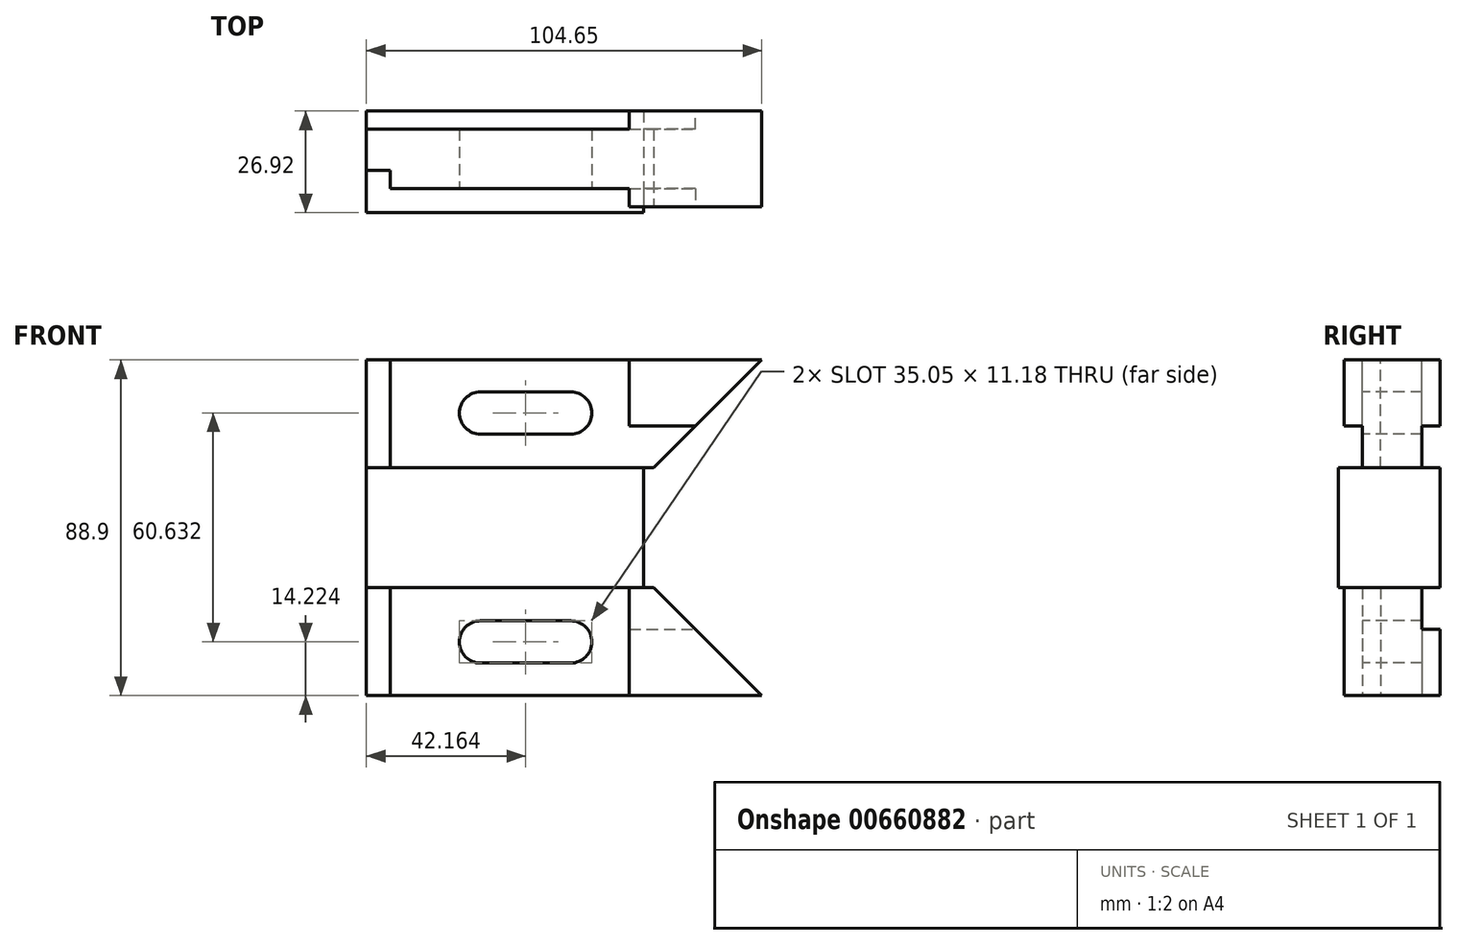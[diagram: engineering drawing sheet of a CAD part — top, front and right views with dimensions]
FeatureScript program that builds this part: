
annotation { "Feature Type Name" : "Feature", "Feature Type Description" : "" }
export const myFeature = defineFeature(function(context is Context, id is Id, definition is map)
    precondition{}
    {
        {
            var Q0;
            Q0=qCreatedBy(makeId("Right.planeOp"),FACE);
            var sketch = newSketch(context, id + "F0", { "sketchPlane" : qUnion([Q0])});
            skLineSegment(sketch, "E0", {"start": v(0, 0) * mm, "end": v(25.4, 0) * mm});
            skLineSegment(sketch, "E1", {"start": v(25.4, 0) * mm, "end": v(25.4, 28.58) * mm});
            skLineSegment(sketch, "E2", {"start": v(0, 0) * mm, "end": v(0, 28.58) * mm});
            skLineSegment(sketch, "E3", {"start": v(25.4, 60.33) * mm, "end": v(25.4, 88.9) * mm});
            skLineSegment(sketch, "E4", {"start": v(0, 60.33) * mm, "end": v(0, 88.9) * mm});
            skLineSegment(sketch, "E5", {"start": v(0, 88.9) * mm, "end": v(25.4, 88.9) * mm});
            skLineSegment(sketch, "E6", {"start": v(0, 28.58) * mm, "end": v(-1.52, 28.58) * mm});
            skLineSegment(sketch, "E7", {"start": v(-1.52, 28.58) * mm, "end": v(-1.52, 60.33) * mm});
            skLineSegment(sketch, "E8", {"start": v(0, 60.33) * mm, "end": v(-1.52, 60.33) * mm});
            skLineSegment(sketch, "E9", {"start": v(25.4, 60.33) * mm, "end": v(26.92, 60.33) * mm});
            skLineSegment(sketch, "E10", {"start": v(25.4, 28.58) * mm, "end": v(26.92, 28.58) * mm});
            skLineSegment(sketch, "E11", {"start": v(26.92, 60.33) * mm, "end": v(26.92, 28.58) * mm});
            skSolve(sketch);
        }
        {
            var Q0;
            Q0=qSketchRegion(id+"F0",true);
            extrude(context, id + "F1", {"entities" : qUnion([Q0]), "depth" : 104.65 * mm, "offsetDistance" : 25 * mm});
        }
        {
            var Q0;
            Q0=makeQuery(id+"F1.opExtrude","SWEPT_FACE",FACE,{"disambiguationData":[OSD([sQuery(id+"F0.wireOp",EDGE,"E5")])]});
            var sketch = newSketch(context, id + "F2", { "sketchPlane" : qUnion([Q0])});
            skLineSegment(sketch, "E12.0.0", {"start": v(0, 0) * mm, "end": v(0, -1.52) * mm});
            skLineSegment(sketch, "E12.0.1", {"start": v(0, -1.52) * mm, "end": v(104.65, -1.52) * mm});
            skLineSegment(sketch, "E12.0.2", {"start": v(104.65, -1.52) * mm, "end": v(104.65, 0) * mm});
            skLineSegment(sketch, "E12.0.3", {"start": v(104.65, 0) * mm, "end": v(0, 0) * mm});
            skLineSegment(sketch, "E13", {"start": v(0, -1.52) * mm, "end": v(0, 4.83) * mm});
            skLineSegment(sketch, "E14.0.0", {"start": v(0, 26.92) * mm, "end": v(0, 25.4) * mm});
            skLineSegment(sketch, "E14.0.1", {"start": v(0, 25.4) * mm, "end": v(104.65, 25.4) * mm});
            skLineSegment(sketch, "E14.0.2", {"start": v(104.65, 25.4) * mm, "end": v(104.65, 26.92) * mm});
            skLineSegment(sketch, "E14.0.3", {"start": v(104.65, 26.92) * mm, "end": v(0, 26.92) * mm});
            skLineSegment(sketch, "E15", {"start": v(0, 26.92) * mm, "end": v(0, 20.57) * mm});
            skLineSegment(sketch, "E16", {"start": v(0, 4.83) * mm, "end": v(0, 9.65) * mm});
            skLineSegment(sketch, "E17", {"start": v(0, 9.65) * mm, "end": v(6.35, 9.65) * mm});
            skLineSegment(sketch, "E18", {"start": v(6.35, 9.65) * mm, "end": v(6.35, 4.83) * mm});
            skLineSegment(sketch, "E19", {"start": v(6.35, 4.83) * mm, "end": v(69.6, 4.83) * mm});
            skLineSegment(sketch, "E20", {"start": v(0, 20.57) * mm, "end": v(69.6, 20.57) * mm});
            skLineSegment(sketch, "E21", {"start": v(69.6, 20.57) * mm, "end": v(69.6, 25.4) * mm});
            skLineSegment(sketch, "E22", {"start": v(69.6, 4.83) * mm, "end": v(69.6, 0) * mm});
            skLineSegment(sketch, "E23", {"start": v(0, -1.52) * mm, "end": v(73.4, -1.52) * mm});
            skLineSegment(sketch, "E24", {"start": v(73.4, -1.52) * mm, "end": v(73.4, 0) * mm});
            skLineSegment(sketch, "E25", {"start": v(73.4, 0) * mm, "end": v(0, 0) * mm});
            skLineSegment(sketch, "E26", {"start": v(0, 25.4) * mm, "end": v(0, 26.92) * mm});
            skLineSegment(sketch, "E27", {"start": v(0, 26.92) * mm, "end": v(73.4, 26.92) * mm});
            skLineSegment(sketch, "E28", {"start": v(73.4, 26.92) * mm, "end": v(73.4, 25.4) * mm});
            skLineSegment(sketch, "E29", {"start": v(73.4, 25.4) * mm, "end": v(0, 25.4) * mm});
            skSolve(sketch);
        }
        {
            var Q0;
            {var subQ0=sQuery(id+"F2.wireOp",EDGE,"E15");Q0=makeQuery(id+"F2.imprint","IMPRINT",FACE,{"disambiguationData":[TD([[makeQuery(id+"F2.imprint","IMPRINT",EDGE,{"derivedFrom":subQ0}),-1.0]])]});}
            var Q1;
            {var subQ0=sQuery(id+"F2.wireOp",EDGE,"E16");Q1=makeQuery(id+"F2.imprint","IMPRINT",FACE,{"disambiguationData":[TD([[makeQuery(id+"F2.imprint","IMPRINT",EDGE,{"derivedFrom":subQ0}),-1.0]])]});}
            extrude(context, id + "F3", {"entities" : qUnion([Q0, Q1]), "operationType" : NewBodyOperationType.REMOVE, "oppositeDirection" : true, "depth" : 28.57 * mm});
        }
        {
            var Q0;
            Q0=makeQuery(id+"F2.imprint","IMPRINT",FACE,{"disambiguationData":[TD([[makeQuery(id+"F2.imprint","IMPRINT",EDGE,{"derivedFrom":sQuery(id+"F2.wireOp",EDGE,"E14.0.1")}),-1.0]])]});
            var Q1;
            Q1=makeQuery(id+"F2.imprint","IMPRINT",FACE,{"disambiguationData":[TD([[makeQuery(id+"F2.imprint","IMPRINT",EDGE,{"derivedFrom":sQuery(id+"F2.wireOp",EDGE,"E12.0.1")}),1.0]])]});
            extrude(context, id + "F4", {"entities" : qUnion([Q0, Q1]), "operationType" : NewBodyOperationType.REMOVE, "oppositeDirection" : true, "depth" : 150.7 * mm, "offsetDistance" : 25 * mm});
        }
        {
            var Q0;
            Q0=makeQuery(id+"F1.opExtrude","SWEPT_FACE",FACE,{"disambiguationData":[OSD([sQuery(id+"F0.wireOp",EDGE,"E0")])]});
            var sketch = newSketch(context, id + "F5", { "sketchPlane" : qUnion([Q0])});
            skLineSegment(sketch, "E30.0", {"start": v(6.35, -4.83) * mm, "end": v(69.6, -4.83) * mm});
            skPoint(sketch, "E31.0", {"position": v(6.35, -9.65) * mm});
            skPoint(sketch, "E32.0", {"position": v(3.18, -9.65) * mm});
            skLineSegment(sketch, "E33.0", {"start": v(0, -9.65) * mm, "end": v(0, -20.57) * mm});
            skLineSegment(sketch, "E34.0", {"start": v(0, -20.57) * mm, "end": v(69.6, -20.57) * mm});
            skLineSegment(sketch, "E35.0", {"start": v(104.65, -25.4) * mm, "end": v(69.6, -25.4) * mm});
            skPoint(sketch, "E36.0", {"position": v(69.6, -22.99) * mm});
            skLineSegment(sketch, "E37.0", {"start": v(104.65, 0) * mm, "end": v(69.6, 0) * mm});
            skLineSegment(sketch, "E38.0", {"start": v(69.6, -4.83) * mm, "end": v(69.6, 0) * mm});
            skLineSegment(sketch, "E39.0", {"start": v(69.6, -20.57) * mm, "end": v(69.6, -25.4) * mm});
            skLineSegment(sketch, "E40.0.0", {"start": v(73.4, -25.4) * mm, "end": v(73.4, -26.92) * mm});
            skLineSegment(sketch, "E40.0.1", {"start": v(73.4, -26.92) * mm, "end": v(0, -26.92) * mm});
            skLineSegment(sketch, "E40.0.2", {"start": v(0, -26.92) * mm, "end": v(0, -20.57) * mm});
            skLineSegment(sketch, "E40.0.5", {"start": v(69.6, -25.4) * mm, "end": v(73.4, -25.4) * mm});
            skLineSegment(sketch, "E41.0.0", {"start": v(73.4, 1.52) * mm, "end": v(73.4, 0) * mm});
            skLineSegment(sketch, "E41.0.1", {"start": v(73.4, 0) * mm, "end": v(69.6, 0) * mm});
            skLineSegment(sketch, "E41.0.2", {"start": v(69.6, 0) * mm, "end": v(69.6, -4.83) * mm});
            skLineSegment(sketch, "E41.0.3", {"start": v(69.6, -4.83) * mm, "end": v(6.35, -4.83) * mm});
            skLineSegment(sketch, "E41.0.4", {"start": v(6.35, -4.83) * mm, "end": v(6.35, -9.65) * mm});
            skLineSegment(sketch, "E41.0.5", {"start": v(6.35, -9.65) * mm, "end": v(0, -9.65) * mm});
            skLineSegment(sketch, "E41.0.6", {"start": v(0, -9.65) * mm, "end": v(0, 1.52) * mm});
            skLineSegment(sketch, "E41.0.7", {"start": v(0, 1.52) * mm, "end": v(73.4, 1.52) * mm});
            skSolve(sketch);
        }
        {
            var Q0;
            Q0=qSketchRegion(id+"F5",true);
            extrude(context, id + "F6", {"entities" : qUnion([Q0]), "operationType" : NewBodyOperationType.REMOVE, "oppositeDirection" : true, "depth" : 28.57 * mm});
        }
        {
            var Q0;
            Q0=makeQuery(id+"F4.boolean.opBoolean","MERGE",FACE,{"derivedFrom":[makeQuery(id+"F1.opExtrude","SWEPT_FACE",FACE,{"disambiguationData":[OSD([sQuery(id+"F0.wireOp",EDGE,"E2")])]}),makeQuery(id+"F1.opExtrude","SWEPT_FACE",FACE,{"disambiguationData":[OSD([sQuery(id+"F0.wireOp",EDGE,"E4")])]}),makeQuery(id+"F4.opExtrude","SWEPT_FACE",FACE,{"disambiguationData":[OSD([sQuery(id+"F2.wireOp",EDGE,"E12.0.3")])]})]});
            var sketch = newSketch(context, id + "F7", { "sketchPlane" : qUnion([Q0])});
            skLineSegment(sketch, "E42.0", {"start": v(104.65, 88.9) * mm, "end": v(69.6, 88.9) * mm});
            skLineSegment(sketch, "E43.0", {"start": v(69.6, 71.37) * mm, "end": v(69.6, 88.9) * mm});
            skLineSegment(sketch, "E44.0", {"start": v(6.35, 88.9) * mm, "end": v(69.6, 88.9) * mm});
            skLineSegment(sketch, "E45.0.0", {"start": v(69.6, 88.9) * mm, "end": v(6.35, 88.9) * mm});
            skLineSegment(sketch, "E45.0.1", {"start": v(6.35, 88.9) * mm, "end": v(6.35, 60.33) * mm});
            skLineSegment(sketch, "E45.0.2", {"start": v(6.35, 60.33) * mm, "end": v(69.6, 60.33) * mm});
            skLineSegment(sketch, "E46.0.0", {"start": v(0, 28.58) * mm, "end": v(73.4, 28.58) * mm});
            skLineSegment(sketch, "E46.0.1", {"start": v(73.4, 28.58) * mm, "end": v(73.4, 60.33) * mm});
            skLineSegment(sketch, "E46.0.2", {"start": v(73.4, 60.33) * mm, "end": v(0, 60.33) * mm});
            skLineSegment(sketch, "E46.0.3", {"start": v(0, 60.33) * mm, "end": v(0, 28.58) * mm});
            skLineSegment(sketch, "E47.0.0", {"start": v(6.35, 0) * mm, "end": v(69.6, 0) * mm});
            skLineSegment(sketch, "E47.0.1", {"start": v(69.6, 0) * mm, "end": v(69.6, 28.58) * mm});
            skLineSegment(sketch, "E47.0.2", {"start": v(69.6, 28.58) * mm, "end": v(6.35, 28.58) * mm});
            skLineSegment(sketch, "E47.0.3", {"start": v(6.35, 28.58) * mm, "end": v(6.35, 0) * mm});
            skLineSegment(sketch, "E48.0.0", {"start": v(73.4, 60.33) * mm, "end": v(73.4, 28.58) * mm});
            skLineSegment(sketch, "E48.0.1", {"start": v(73.4, 28.58) * mm, "end": v(69.6, 28.58) * mm});
            skLineSegment(sketch, "E48.0.2", {"start": v(69.6, 28.58) * mm, "end": v(69.6, 0) * mm});
            skLineSegment(sketch, "E48.0.3", {"start": v(69.6, 0) * mm, "end": v(104.65, 0) * mm});
            skLineSegment(sketch, "E48.0.4", {"start": v(104.65, 0) * mm, "end": v(104.65, 88.9) * mm});
            skLineSegment(sketch, "E48.0.6", {"start": v(69.6, 88.9) * mm, "end": v(69.6, 60.33) * mm});
            skLineSegment(sketch, "E48.0.7", {"start": v(69.6, 60.33) * mm, "end": v(73.4, 60.33) * mm});
            skPoint(sketch, "E49.0", {"position": v(0, 14.29) * mm});
            skPoint(sketch, "E50.0", {"position": v(0, 74.61) * mm});
            skLineSegment(sketch, "E51.0", {"start": v(0, 60.33) * mm, "end": v(0, 88.9) * mm});
            skLineSegment(sketch, "E52.0", {"start": v(0, 88.9) * mm, "end": v(6.35, 88.9) * mm});
            skLineSegment(sketch, "E53", {"start": v(0, 88.9) * mm, "end": v(69.6, 88.9) * mm});
            skLineSegment(sketch, "E54", {"start": v(69.6, 88.9) * mm, "end": v(69.6, 71.37) * mm});
            skLineSegment(sketch, "E55", {"start": v(69.6, 71.37) * mm, "end": v(87.12, 71.37) * mm});
            skLineSegment(sketch, "E56", {"start": v(104.65, 88.9) * mm, "end": v(76.07, 60.33) * mm});
            skLineSegment(sketch, "E57", {"start": v(73.4, 60.33) * mm, "end": v(76.07, 60.33) * mm});
            skLineSegment(sketch, "E58", {"start": v(69.6, 0) * mm, "end": v(69.6, 14.29) * mm});
            skLineSegment(sketch, "E59", {"start": v(104.65, 44.45) * mm, "end": v(0, 44.45) * mm});
            skLineSegment(sketch, "E60.MirrorCS", {"start": v(104.65, 0) * mm, "end": v(76.07, 28.58) * mm});
            skLineSegment(sketch, "E61.MirrorCS", {"start": v(73.4, 28.58) * mm, "end": v(76.07, 28.58) * mm});
            skLineSegment(sketch, "E62.MirrorCS", {"start": v(69.6, 17.53) * mm, "end": v(87.12, 17.53) * mm});
            skSolve(sketch);
        }
        {
            var Q0;
            {var subQ5=sQuery(id+"F7.wireOp",EDGE,"E57");Q0=makeQuery(id+"F7.imprint","IMPRINT",FACE,{"disambiguationData":[TD([[makeQuery(id+"F7.imprint","IMPRINT",EDGE,{"derivedFrom":subQ5}),-1.0]])]});}
            var Q1;
            {var subQ8=sQuery(id+"F7.wireOp",EDGE,"E61.MirrorCS");Q1=makeQuery(id+"F7.imprint","IMPRINT",FACE,{"disambiguationData":[TD([[makeQuery(id+"F7.imprint","IMPRINT",EDGE,{"derivedFrom":subQ8}),1.0]])]});}
            extrude(context, id + "F8", {"entities" : qUnion([Q0, Q1]), "operationType" : NewBodyOperationType.REMOVE, "endBound" : BoundingType.THROUGH_ALL, "oppositeDirection" : true, "depth" : 25.4 * mm});
        }
        {
            var Q0;
            Q0=makeQuery(id+"F7.imprint","IMPRINT",FACE,{"disambiguationData":[TD([[makeQuery(id+"F7.imprint","IMPRINT",EDGE,{"derivedFrom":sQuery(id+"F7.wireOp",EDGE,"E48.0.6")}),-1.0]])]});
            var Q1;
            {var subQ1=sQuery(id+"F7.wireOp",EDGE,"E48.0.1");Q1=makeQuery(id+"F7.imprint","IMPRINT",FACE,{"disambiguationData":[TD([[makeQuery(id+"F7.imprint","IMPRINT",EDGE,{"derivedFrom":subQ1}),1.0]])]});}
            extrude(context, id + "F9", {"entities" : qUnion([Q0, Q1]), "operationType" : NewBodyOperationType.REMOVE, "oppositeDirection" : true, "depth" : 4.83 * mm});
        }
        {
            var Q0;
            Q0=makeQuery(id+"F8.boolean.opBoolean","SPLIT",FACE,{"disambiguationData":[TD([makeQuery(id+"F1.opExtrude","SWEPT_FACE",FACE,{"disambiguationData":[OSD([sQuery(id+"F0.wireOp",EDGE,"E0")])]})])],"derivedFrom":makeQuery(id+"F4.boolean.opBoolean","MERGE",FACE,{"derivedFrom":[makeQuery(id+"F1.opExtrude","SWEPT_FACE",FACE,{"disambiguationData":[OSD([sQuery(id+"F0.wireOp",EDGE,"E1")])]}),makeQuery(id+"F1.opExtrude","SWEPT_FACE",FACE,{"disambiguationData":[OSD([sQuery(id+"F0.wireOp",EDGE,"E3")])]}),makeQuery(id+"F4.opExtrude","SWEPT_FACE",FACE,{"disambiguationData":[OSD([sQuery(id+"F2.wireOp",EDGE,"E14.0.1")])]})]})});
            var sketch = newSketch(context, id + "F10", { "sketchPlane" : qUnion([Q0])});
            skLineSegment(sketch, "E63.0", {"start": v(-69.6, 71.37) * mm, "end": v(-87.12, 71.37) * mm});
            skLineSegment(sketch, "E64.0", {"start": v(-104.65, 88.9) * mm, "end": v(-76.07, 60.33) * mm});
            skLineSegment(sketch, "E65.0.0", {"start": v(-69.6, 60.33) * mm, "end": v(-73.4, 60.33) * mm});
            skLineSegment(sketch, "E65.0.1", {"start": v(-73.4, 60.33) * mm, "end": v(-76.07, 60.33) * mm});
            skLineSegment(sketch, "E65.0.2", {"start": v(-76.07, 60.33) * mm, "end": v(-87.12, 71.37) * mm});
            skLineSegment(sketch, "E65.0.3", {"start": v(-87.12, 71.37) * mm, "end": v(-69.6, 71.37) * mm});
            skLineSegment(sketch, "E65.0.4", {"start": v(-69.6, 71.37) * mm, "end": v(-69.6, 60.33) * mm});
            skLineSegment(sketch, "E66.0.0", {"start": v(-69.6, 28.58) * mm, "end": v(-69.6, 17.53) * mm});
            skLineSegment(sketch, "E66.0.1", {"start": v(-69.6, 17.53) * mm, "end": v(-87.12, 17.53) * mm});
            skLineSegment(sketch, "E66.0.2", {"start": v(-87.12, 17.53) * mm, "end": v(-76.07, 28.58) * mm});
            skLineSegment(sketch, "E66.0.3", {"start": v(-76.07, 28.58) * mm, "end": v(-73.4, 28.58) * mm});
            skLineSegment(sketch, "E66.0.4", {"start": v(-73.4, 28.58) * mm, "end": v(-69.6, 28.58) * mm});
            skSolve(sketch);
        }
        {
            var Q0;
            Q0=qSketchRegion(id+"F10",true);
            extrude(context, id + "F11", {"entities" : qUnion([Q0]), "operationType" : NewBodyOperationType.REMOVE, "oppositeDirection" : true, "depth" : 4.83 * mm});
        }
        {
            var Q0;
            Q0=makeQuery(id+"F7.imprint","IMPRINT",FACE,{"disambiguationData":[TD([[makeQuery(id+"F7.imprint","IMPRINT",EDGE,{"derivedFrom":sQuery(id+"F7.wireOp",EDGE,"E47.0.0")}),1.0]])]});
            var sketch = newSketch(context, id + "F12", { "sketchPlane" : qUnion([Q0])});
            skLineSegment(sketch, "E67", {"start": v(0, 0) * mm, "end": v(0, 14.22) * mm});
            skLineSegment(sketch, "E68", {"start": v(0, 0) * mm, "end": v(24.64, 0) * mm});
            skLineSegment(sketch, "E69", {"start": v(24.64, 0) * mm, "end": v(24.64, 14.22) * mm});
            skLineSegment(sketch, "E70", {"start": v(24.64, 14.22) * mm, "end": v(59.69, 14.22) * mm});
            skLineSegment(sketch, "E71", {"start": v(24.64, 14.22) * mm, "end": v(30.23, 14.22) * mm});
            skCircle(sketch, "E72", {"center": v(30.23, 14.22) * mm, "radius": 5.59 * mm});
            skCircle(sketch, "E73", {"center": v(54.1, 14.22) * mm, "radius": 5.59 * mm});
            skLineSegment(sketch, "E74", {"start": v(30.23, 19.81) * mm, "end": v(54.1, 19.81) * mm});
            skLineSegment(sketch, "E75", {"start": v(30.23, 8.64) * mm, "end": v(54.1, 8.64) * mm});
            skLineSegment(sketch, "E76", {"start": v(0, 44.54) * mm, "end": v(88.44, 44.54) * mm});
            skCircle(sketch, "E77.MirrorC", {"center": v(54.1, 74.86) * mm, "radius": 5.59 * mm});
            skLineSegment(sketch, "E78.MirrorCS", {"start": v(24.64, 74.86) * mm, "end": v(59.69, 74.86) * mm});
            skCircle(sketch, "E79.MirrorC", {"center": v(30.23, 74.86) * mm, "radius": 5.59 * mm});
            skLineSegment(sketch, "E80.MirrorCS", {"start": v(30.23, 80.44) * mm, "end": v(54.1, 80.44) * mm});
            skLineSegment(sketch, "E81.MirrorCS", {"start": v(30.23, 69.27) * mm, "end": v(54.1, 69.27) * mm});
            skSolve(sketch);
        }
        {
            var Q0;
            Q0=qSketchRegion(id+"F12",true);
            extrude(context, id + "F13", {"entities" : qUnion([Q0]), "operationType" : NewBodyOperationType.REMOVE, "endBound" : BoundingType.THROUGH_ALL, "oppositeDirection" : true, "depth" : 25.4 * mm});
        }
    });
